# Revit family: WashBasin-80cm-VanityWashbasin-Vitra-S50Series-5408
name_source: partatom
category: Plumbing Fixtures
revit_build: Autodesk Revit 2017 (Build: 20160225_1515(x64)
units: mm (PartAtom-declared; Revit-internal decimal feet)

## family parameters
Cut with Voids When Loaded = No
Host = Face
OmniClass Number = 23.45.05.14.14
OmniClass Title = Sinks/Lavatories
Part Type = Normal
Room Calculation Point = No
Round Connector Dimension = Use Diameter
Shared = Yes

## types (2) — shared parameters
BIMobject category = Sanitary - Basins
Brand = VitrA
CW Connection = Yes
Color = White
Default Elevation = 850 mm  [stored 2.78871 ft]
Description = VitrA S50 Vanity Washbasin - With Tap Hole - With Overflow Hole - 80cm - White
Design country = Turkey
HW Connection = Yes
IFC Classification = Sanitary Terminal
Main Material = Ceramic
Manufacturer = Vitra
Manufacturer name = Vitra
Masterformat 2014 Code = 22 41 16
Masterformat 2014 Description = Residential Lavatories and Sinks
Mounting type = Wall Hung
NBS Referans Code = 35-65-70-94
NBS Referans Description = Wash Basin Systems
Nominal Depth (mm) = 465 mm  [stored 1.52559 ft]
Nominal Height (mm) = 210 mm
Nominal Width (mm) = 800 mm  [stored 2.62467 ft]
OmniClass Code = 23.45.05.14.14
OmniClass Description = Sinks/Lavatories
Primary Material = White
Product certification = https://www.vitraglobal.com
Product family = Vanity WashBasin
Product group = S50 Series
URL = https://vitraglobal.com
Uniclass 1.4 Code = L7212
Uniclass 1.4 Description = Washbasins
Uniclass 2.0 Code = SS-35-65-70-94
Uniclass 2.0 Description = Sanitary Dispensing And Disposal Units
Uniclass 2015 Code = Pr_40_20_96_81
Uniclass 2015 Name = Wash basins, Sinks and troughs
Uniformat II Code = D2010
Uniformat II Description = Plumbing Fixtures
Vent Connection = No
Warranty Period (Year) = 10 Years
Waste Connection = Yes
Weight Net (kg) = 26
Youtube = https://www.youtube.com

## per-type parameters (varying)
| type | Article No. (default) | Model | Product SKU | Product url | Technical description |
| WashBasin-80cm-VanityWashbasin-Vitra-S50Series-5408B003-0001 | 5408B003-0001 | 5408B003-0001 | 5408B003-0001 | https://www.vitraglobal.com | https://www.vitraglobal.com |
| WashBasin-80cm-VanityWashbasin-Vitra-S50Series-5408B003H0001 | 5408B003H0001 | 5408B003H0001 | 5408B003H0001 | https://www.vitra-india.com | https://www.vitra-india.com |

note: [stored X ft] marks values corroborated as IEEE doubles in the binary element streams (Revit-internal decimal feet)

## geometry (parser evidence)
native form markers: Sweep x3
no freeform markers — native parametric forms only
